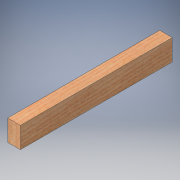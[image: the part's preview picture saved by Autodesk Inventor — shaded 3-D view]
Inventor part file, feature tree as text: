
AUTODESK INVENTOR PART (.ipt)
format: ipt  version: 2016 SP1 (Build 200210100, 210)  size: 102,912 bytes
history: native  units: in
note: dims shown in document units (in); Inventor stores cm internally (conversion verified against a paired STEP export)
features: extrude x1, sketch x1
ambient origin geometry x8: Origin, YZ Plane, XZ Plane, XY Plane, X Axis, Y Axis, Z Axis, Center Point
bodies: Solid1 (feature_tree)
feature tree (2):
  extrude  "Extrusion1"  Depth=2.5in
  sketch  "Sketch1"  dims[d0=1.5in d1=2.5in d2=18.0in d3=0.0in]
